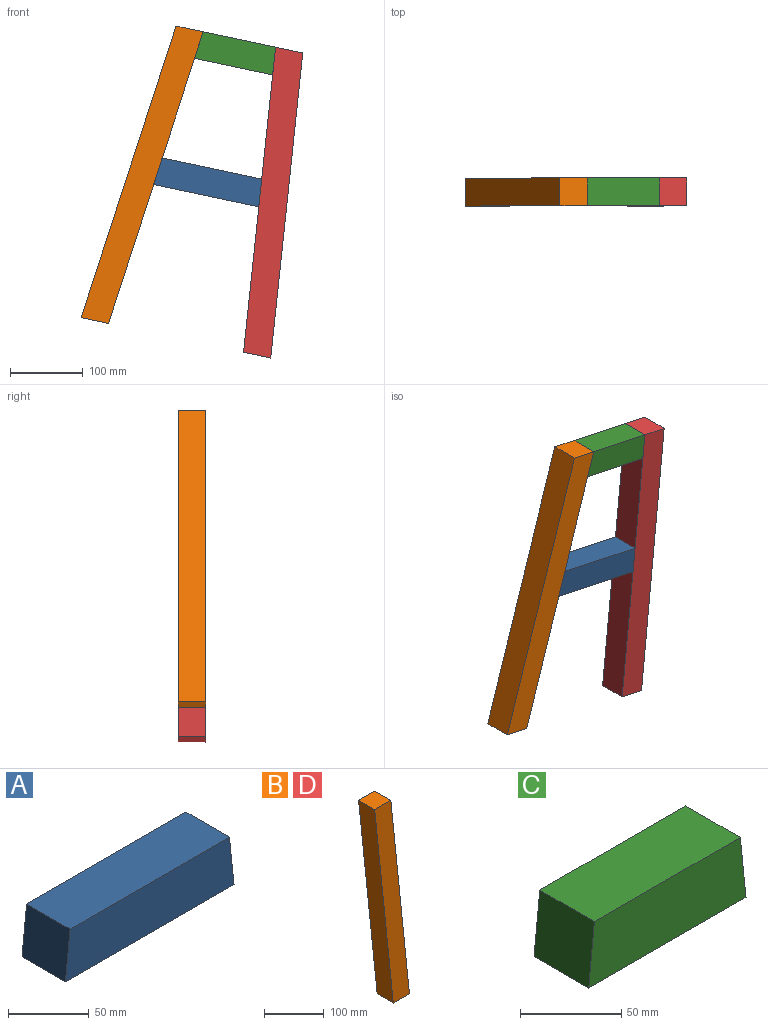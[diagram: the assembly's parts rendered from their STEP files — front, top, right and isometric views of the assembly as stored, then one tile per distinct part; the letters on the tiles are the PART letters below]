
ASSEMBLY  parts=4 mates=5
PART A: 6 faces, bbox 147.7x38.1x38.1 mm
  f0: plane 139.7x38.1mm, normal (0,0,1), area 5322.6mm2, adj f1,f3,f4,f5
  f1: plane 38.1x38.1mm, normal (-0.99,0,0.1), area 1459.6mm2, adj f0,f2,f4,f5
  f2: plane 147.71x38.1mm, normal (0,0,-1), area 5627.7mm2, adj f1,f3,f4,f5
  f3: plane 38.1x38.1mm, normal (0.99,0,0.1), area 1459.6mm2, adj f0,f2,f4,f5
  f4: plane 147.71x38.1mm, normal (0,-1,0), area 5475.1mm2, adj f0,f1,f2,f3
  f5: plane 147.71x38.1mm, normal (0,1,0), area 5475.1mm2, adj f0,f1,f2,f3
PART B: 6 faces, bbox 82.4x38.1x419.1 mm
  f0: plane 38.31x38.1mm, normal (0,0,1), area 1459.6mm2, adj f1,f3,f4,f5
  f1: plane 419.1x44.05mm, normal (-0.99,0,-0.1), area 16055.7mm2, adj f0,f2,f4,f5
  f2: plane 38.31x38.1mm, normal (0,0,-1), area 1459.6mm2, adj f1,f3,f4,f5
  f3: plane 419.1x44.05mm, normal (0.99,0,0.1), area 16055.7mm2, adj f0,f2,f4,f5
  f4: plane 419.1x82.36mm, normal (0,-1,0), area 16055.7mm2, adj f0,f1,f2,f3
  f5: plane 419.1x82.36mm, normal (0,1,0), area 16055.7mm2, adj f0,f1,f2,f3
PART C: 6 faces, bbox 109.6x38.1x38.1 mm
  f0: plane 101.6x38.1mm, normal (0,0,1), area 3871mm2, adj f1,f3,f4,f5
  f1: plane 38.1x38.1mm, normal (-0.99,0,0.1), area 1459.6mm2, adj f0,f2,f4,f5
  f2: plane 109.61x38.1mm, normal (0,0,-1), area 4176.1mm2, adj f1,f3,f4,f5
  f3: plane 38.1x38.1mm, normal (0.99,0,0.1), area 1459.6mm2, adj f0,f2,f4,f5
  f4: plane 109.61x38.1mm, normal (0,-1,0), area 4023.5mm2, adj f0,f1,f2,f3
  f5: plane 109.61x38.1mm, normal (0,1,0), area 4023.5mm2, adj f0,f1,f2,f3
PART D: same geometry as B
PLACE A rot(axis=(-0.1,0,-0.99),180deg) t=(-85.37,9.14,-97.86)mm
PLACE B rot(axis=(-0.1,0,-0.99),180deg) t=(-165.7,9.14,104.52)mm
PLACE C rot(axis=(-0.1,0,-0.99),180deg) t=(-66.32,9.14,83.39)mm
PLACE D rot(axis=(0,1,0),12deg) t=(-66.32,47.24,83.39)mm
MATE planar A.f5 <-> B.f5  axis (0,-1,0) through (-227.94,9.14,-87.03)mm
MATE fastened B.f1 <-> C.f3  axis (0.95,0,-0.31) through (-165.7,28.19,104.52)mm
MATE planar A.f3 <-> B.f1  axis (-0.95,0,0.31) through (-227.94,28.19,-87.03)mm
MATE fastened C.f1 <-> D.f1  axis (0.99,0,-0.1) through (-66.32,28.19,83.39)mm
MATE planar D.f1 <-> A.f1  axis (-0.99,0,0.1) through (-88.35,28.19,-126.16)mm
